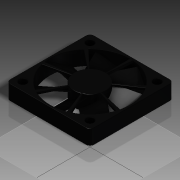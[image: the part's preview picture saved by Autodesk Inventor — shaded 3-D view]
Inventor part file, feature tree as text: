
AUTODESK INVENTOR PART (.ipt)
format: ipt  version: 2013 (Build 170138000, 138)  size: 439,808 bytes
history: native  units: in
note: dims shown in document units (in); Inventor stores cm internally (conversion verified against a paired STEP export)
features: sketch x6, extrude x4, plane x1, pattern_circular x1, fillet x1, projected_geometry x1
ambient origin geometry x8: Origin, YZ Plane, XZ Plane, XY Plane, X Axis, Y Axis, Z Axis, Center Point
bodies: Solid1 (feature_tree)
feature tree (14):
  extrude  "Extrusion1"  Depth=1.5748in
  extrude  "Extrusion2"  Depth=1.5748in
  extrude  "Extrusion3"  Depth=1.2598in
  sketch  "Sketch4"  dims[d7=1.2598in d8=0.1378in]
  plane  "Work Plane1"
  extrude  "Extrusion4"  Depth=0.1378in
  sketch  "Sketch6"  dims[d10=0.0787in d11=1.4961in d12=0.2756in d13=0.0in d14=0.0787in d15=0.0787in d16=0.5906in d22=0.0394in d23=0.0in d25=0.0344in d30=2.7559in d32=360.0deg d37=60.0deg d38=0.0157in d41=0.0079in d43=0.7402in d44=0.0in d45=0.0079in d46=0.2716in d48=2.7559in d49=360.0deg d51=0.0079in]
  pattern_circular  "Circular Pattern1"  [2 undecoded]
  fillet  "Fillet1"  Radius=0.2756in
  sketch  "Sketch1"  dims[d0=1.5748in d1=1.5748in]
  sketch  "Sketch2"  dims[d2=0.3937in d3=0.0in d4=1.5748in]
  sketch  "Sketch3"  dims[d5=1.5748in d6=1.2598in]
  sketch  "Sketch5"  dims[d9=0.0787in]
  projected_geometry  "Projected Loop1"
note: 2 required parameter values undecoded (feature->parameter linkage not recoverable at this tier; creation-order binding heuristic only, values carry confidence <= 0.55)
